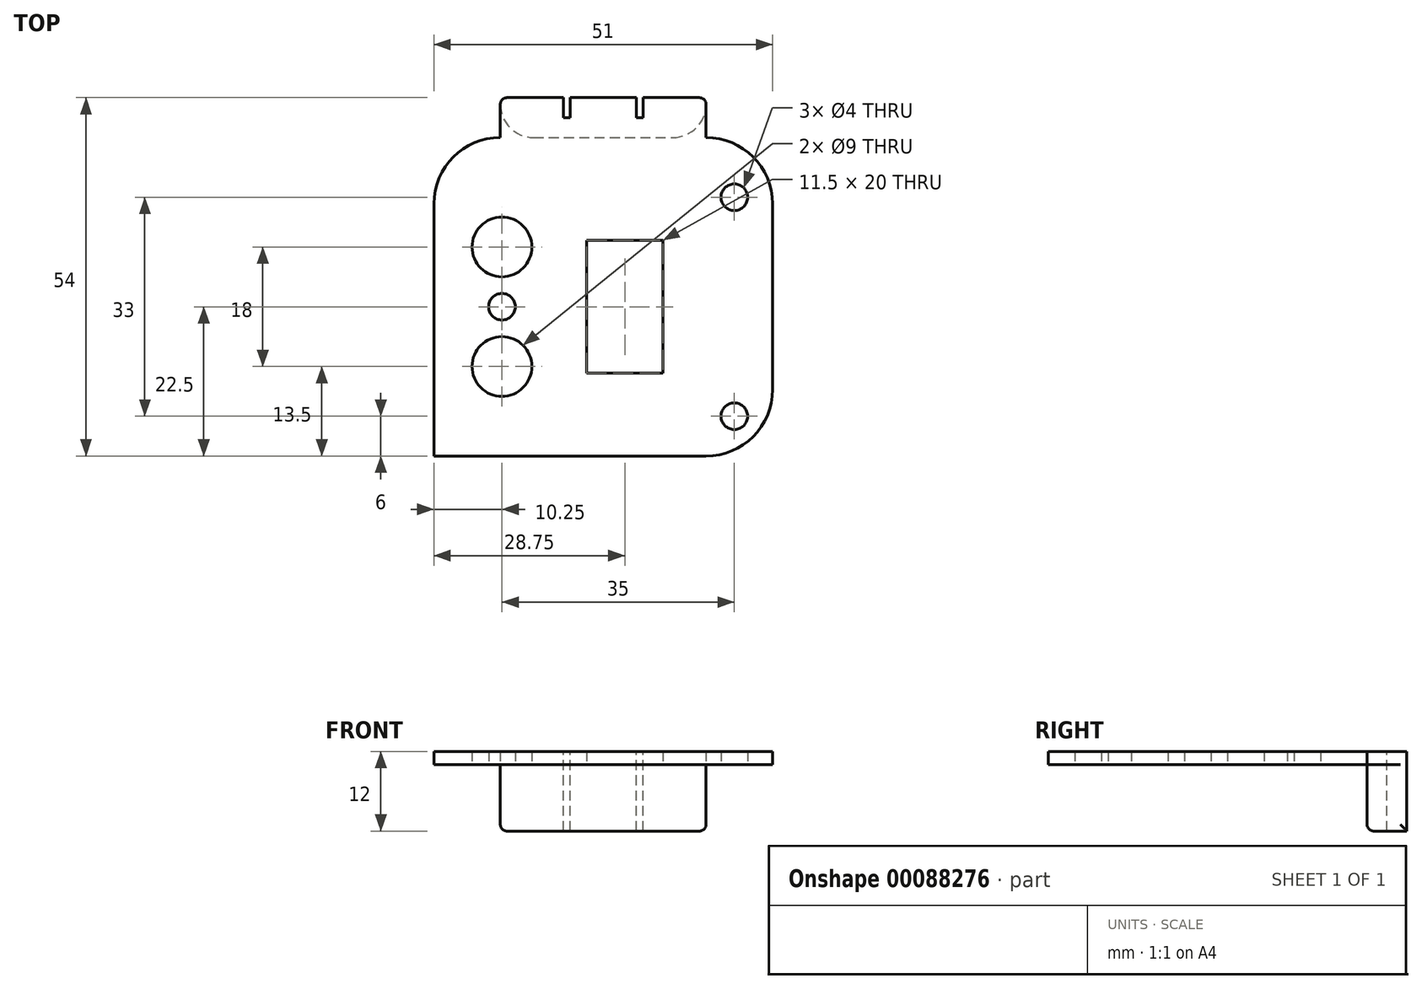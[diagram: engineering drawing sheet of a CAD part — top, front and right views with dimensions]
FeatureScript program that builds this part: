
annotation { "Feature Type Name" : "Feature", "Feature Type Description" : "" }
export const myFeature = defineFeature(function(context is Context, id is Id, definition is map)
    precondition{}
    {
        {
            var Q0;
            Q0=qCreatedBy(makeId("Top.planeOp"),FACE);
            var sketch = newSketch(context, id + "F0", { "sketchPlane" : qUnion([Q0])});
            skLineSegment(sketch, "E0.bottom", {"start": v(0, 0) * mm, "end": v(51, 0) * mm});
            skLineSegment(sketch, "E0.top", {"start": v(0, 48) * mm, "end": v(51, 48) * mm});
            skLineSegment(sketch, "E0.left", {"start": v(0, 0) * mm, "end": v(0, 48) * mm});
            skLineSegment(sketch, "E0.right", {"start": v(51, 0) * mm, "end": v(51, 48) * mm});
            skPoint(sketch, "E1", {"position": v(10.25, 22.5) * mm});
            skCircle(sketch, "E2", {"center": v(10.25, 22.5) * mm, "radius": 2 * mm});
            skPoint(sketch, "E3", {"position": v(23, 12.5) * mm});
            skLineSegment(sketch, "E4.bottom", {"start": v(23, 12.5) * mm, "end": v(34.5, 12.5) * mm});
            skLineSegment(sketch, "E4.top", {"start": v(23, 32.5) * mm, "end": v(34.5, 32.5) * mm});
            skLineSegment(sketch, "E4.left", {"start": v(23, 12.5) * mm, "end": v(23, 32.5) * mm});
            skLineSegment(sketch, "E4.right", {"start": v(34.5, 12.5) * mm, "end": v(34.5, 32.5) * mm});
            skPoint(sketch, "E5", {"position": v(10.25, 31.5) * mm});
            skPoint(sketch, "E6", {"position": v(10.25, 13.5) * mm});
            skCircle(sketch, "E7", {"center": v(10.25, 31.5) * mm, "radius": 4.5 * mm});
            skCircle(sketch, "E8", {"center": v(10.25, 13.5) * mm, "radius": 4.5 * mm});
            skPoint(sketch, "E9", {"position": v(45.25, 6) * mm});
            skPoint(sketch, "E10", {"position": v(45.25, 39) * mm});
            skCircle(sketch, "E11", {"center": v(45.25, 39) * mm, "radius": 2 * mm});
            skCircle(sketch, "E12", {"center": v(45.25, 6) * mm, "radius": 2 * mm});
            skSolve(sketch);
        }
        {
            var Q0;
            Q0 = qSketchRegion(id + "F0", true);
            extrude(context, id + "F1", {"entities" : qUnion([Q0]), "depth" : 2 * mm});
        }
        {
            var Q0;
            Q0=makeQuery(id+"F1.opExtrude","SWEPT_FACE",FACE,{"disambiguationData":[OSD([sQuery(id+"F0.wireOp",EDGE,"E0.top")])]});
            var sketch = newSketch(context, id + "F2", { "sketchPlane" : qUnion([Q0])});
            skLineSegment(sketch, "E13.bottom", {"start": v(-41, 2) * mm, "end": v(-10, 2) * mm});
            skLineSegment(sketch, "E13.top", {"start": v(-41, -10) * mm, "end": v(-10, -10) * mm});
            skLineSegment(sketch, "E13.left", {"start": v(-41, 2) * mm, "end": v(-41, 0) * mm});
            skLineSegment(sketch, "E13.right", {"start": v(-10, 2) * mm, "end": v(-10, 0) * mm});
            skLineSegment(sketch, "E14", {"start": v(-10, 0) * mm, "end": v(-10, -10) * mm});
            skLineSegment(sketch, "E15", {"start": v(-41, 0) * mm, "end": v(-41, -10) * mm});
            skSolve(sketch);
        }
        {
            var Q0;
            Q0 = qSketchRegion(id + "F2", true);
            extrude(context, id + "F3", {"entities" : qUnion([Q0]), "operationType" : NewBodyOperationType.ADD, "depth" : 6 * mm});
        }
        {
            var Q0;
            Q0=makeQuery(id+"F3.opExtrude","CAP_FACE",FACE,{"disambiguationData":[OSD([sQuery(id+"F2.wireOp",EDGE,"E13.bottom"),sQuery(id+"F2.wireOp",EDGE,"E13.top"),sQuery(id+"F2.wireOp",EDGE,"E13.left"),sQuery(id+"F2.wireOp",EDGE,"E13.right"),sQuery(id+"F2.wireOp",EDGE,"E14"),sQuery(id+"F2.wireOp",EDGE,"E15")])],"isStart":false});
            var sketch = newSketch(context, id + "F4", { "sketchPlane" : qUnion([Q0])});
            skPoint(sketch, "E16", {"position": v(-25.5, -10) * mm});
            skLineSegment(sketch, "E17.bottom", {"start": v(-20.5, -10) * mm, "end": v(-19.5, -10) * mm});
            skLineSegment(sketch, "E17.top", {"start": v(-20.5, 2) * mm, "end": v(-19.5, 2) * mm});
            skLineSegment(sketch, "E17.left", {"start": v(-20.5, -10) * mm, "end": v(-20.5, 2) * mm});
            skLineSegment(sketch, "E17.right", {"start": v(-19.5, -10) * mm, "end": v(-19.5, 2) * mm});
            skLineSegment(sketch, "E18.bottom", {"start": v(-30.5, -10) * mm, "end": v(-31.5, -10) * mm});
            skLineSegment(sketch, "E18.top", {"start": v(-30.5, 2) * mm, "end": v(-31.5, 2) * mm});
            skLineSegment(sketch, "E18.left", {"start": v(-30.5, -10) * mm, "end": v(-30.5, 2) * mm});
            skLineSegment(sketch, "E18.right", {"start": v(-31.5, -10) * mm, "end": v(-31.5, 2) * mm});
            skSolve(sketch);
        }
        {
            var Q0;
            Q0 = qSketchRegion(id + "F4", true);
            extrude(context, id + "F5", {"entities" : qUnion([Q0]), "operationType" : NewBodyOperationType.REMOVE, "oppositeDirection" : true, "depth" : 3 * mm});
        }
        {
            var Q0;
            {var subQ13=sQuery(id+"F2.wireOp",EDGE,"E13.bottom");var subQ14=sQuery(id+"F2.wireOp",EDGE,"E14");var subQ15=sQuery(id+"F2.wireOp",EDGE,"E13.right");Q0=makeQuery(id+"F3.boolean.opBoolean","SPLIT",EDGE,{"disambiguationData":[TD([makeQuery(id+"F3.opExtrude","SWEPT_FACE",FACE,{"disambiguationData":[OSD([subQ13])]})])],"derivedFrom":makeQuery(id+"F3.opExtrude","CAP_EDGE",EDGE,{"disambiguationData":[OSD([subQ15,subQ14])],"isStart":true})});}
            var Q1;
            {var subQ13=sQuery(id+"F2.wireOp",EDGE,"E13.bottom");var subQ14=sQuery(id+"F2.wireOp",EDGE,"E15");var subQ15=sQuery(id+"F2.wireOp",EDGE,"E13.left");Q1=makeQuery(id+"F3.boolean.opBoolean","SPLIT",EDGE,{"disambiguationData":[TD([makeQuery(id+"F3.opExtrude","SWEPT_FACE",FACE,{"disambiguationData":[OSD([subQ13])]})])],"derivedFrom":makeQuery(id+"F3.opExtrude","CAP_EDGE",EDGE,{"disambiguationData":[OSD([subQ15,subQ14])],"isStart":true})});}
            fillet(context, id + "F6", {"entities" : qUnion([Q0, Q1]), "radius" : 5 * mm, "tangentPropagation" : true, "allowEdgeOverflow" : false});
        }
        {
            var Q0;
            Q0=makeQuery(id+"F3.opExtrude","CAP_EDGE",EDGE,{"disambiguationData":[OSD([sQuery(id+"F2.wireOp",EDGE,"E13.left"),sQuery(id+"F2.wireOp",EDGE,"E15")])],"isStart":false});
            var Q1;
            Q1=makeQuery(id+"F3.opExtrude","CAP_EDGE",EDGE,{"disambiguationData":[OSD([sQuery(id+"F2.wireOp",EDGE,"E13.right"),sQuery(id+"F2.wireOp",EDGE,"E14")])],"isStart":false});
            var Q2;
            Q2=makeQuery(id+"F3.opExtrude","SWEPT_EDGE",EDGE,{"disambiguationData":[OSD([sQuery(id+"F2.wireOp",EDGE,"E13.top"),sQuery(id+"F2.wireOp",EDGE,"E14")])]});
            var Q3;
            Q3=makeQuery(id+"F3.opExtrude","SWEPT_EDGE",EDGE,{"disambiguationData":[OSD([sQuery(id+"F2.wireOp",EDGE,"E13.top"),sQuery(id+"F2.wireOp",EDGE,"E15")])]});
            fillet(context, id + "F7", {"entities" : qUnion([Q0, Q1, Q2, Q3]), "radius" : 1 * mm, "tangentPropagation" : true, "allowEdgeOverflow" : false});
        }
        {
            var Q0;
            Q0=makeQuery(id+"F1.opExtrude","SWEPT_EDGE",EDGE,{"disambiguationData":[OSD([sQuery(id+"F0.wireOp",EDGE,"E0.top"),sQuery(id+"F0.wireOp",EDGE,"E0.right")])]});
            var Q1;
            Q1=makeQuery(id+"F1.opExtrude","SWEPT_EDGE",EDGE,{"disambiguationData":[OSD([sQuery(id+"F0.wireOp",EDGE,"E0.top"),sQuery(id+"F0.wireOp",EDGE,"E0.left")])]});
            var Q2;
            Q2=makeQuery(id+"F1.opExtrude","SWEPT_EDGE",EDGE,{"disambiguationData":[OSD([sQuery(id+"F0.wireOp",EDGE,"E0.bottom"),sQuery(id+"F0.wireOp",EDGE,"E0.right")])]});
            fillet(context, id + "F8", {"entities" : qUnion([Q0, Q1, Q2]), "radius" : 10 * mm, "tangentPropagation" : true, "allowEdgeOverflow" : false});
        }
    });
